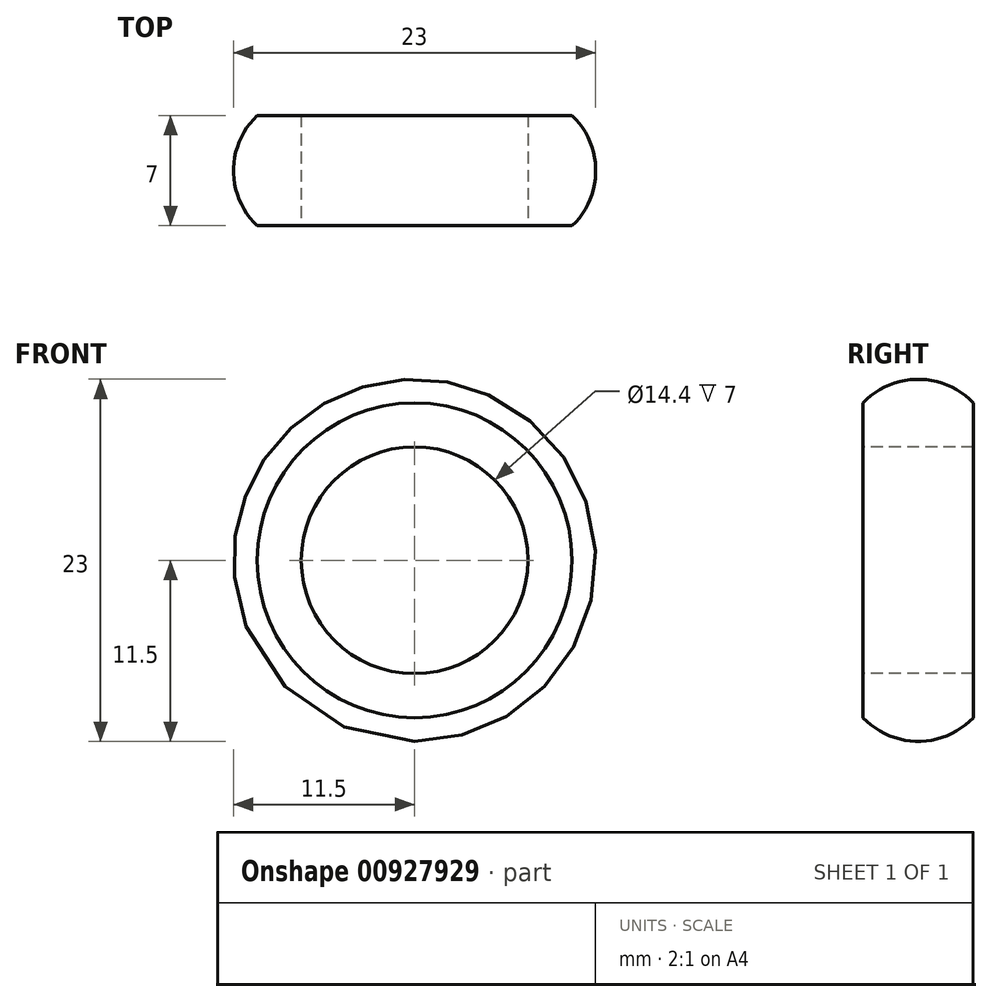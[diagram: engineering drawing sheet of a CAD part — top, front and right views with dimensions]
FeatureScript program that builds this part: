
annotation { "Feature Type Name" : "Feature", "Feature Type Description" : "" }
export const myFeature = defineFeature(function(context is Context, id is Id, definition is map)
    precondition{}
    {
        {
            var Q0;
            Q0=qCreatedBy(makeId("Right.planeOp"),FACE);
            var sketch = newSketch(context, id + "F0", { "sketchPlane" : qUnion([Q0])});
            skLineSegment(sketch, "E0", {"start": v(-3.5, 7.2) * mm, "end": v(3.5, 7.2) * mm});
            skLineSegment(sketch, "E1", {"start": v(-3.5, 7.2) * mm, "end": v(-3.5, 10) * mm});
            skLineSegment(sketch, "E2", {"start": v(3.5, 7.2) * mm, "end": v(3.5, 10) * mm});
            skArc(sketch, "E3", {"start": v(-3.5, 10) * mm, "mid": v(-1.9, 11.1) * mm, "end": v(0, 11.5) * mm});
            skArc(sketch, "E4", {"start": v(3.5, 10) * mm, "mid": v(1.9, 11.1) * mm, "end": v(0, 11.5) * mm});
            skLineSegment(sketch, "E5", {"start": v(-6.83, 0) * mm, "end": v(6.83, 0) * mm, "construction": true});
            skSolve(sketch);
        }
        {
            var Q0;
            Q0=makeQuery(id+"F0.imprint","IMPRINT",FACE,{"disambiguationData":[TD([[makeQuery(id+"F0.imprint","IMPRINT",EDGE,{"derivedFrom":sQuery(id+"F0.wireOp",EDGE,"E0")}),1.0]])]});
            var Q1;
            Q1=sQuery(id+"F0.wireOp",EDGE,"E5");
            revolve(context, id + "F1", {"surfaceOperationType" : NewSurfaceOperationType.NEW, "entities" : qUnion([Q0]), "axis" : qUnion([Q1]), "revolveType" : RevolveType.FULL});
        }
    });
